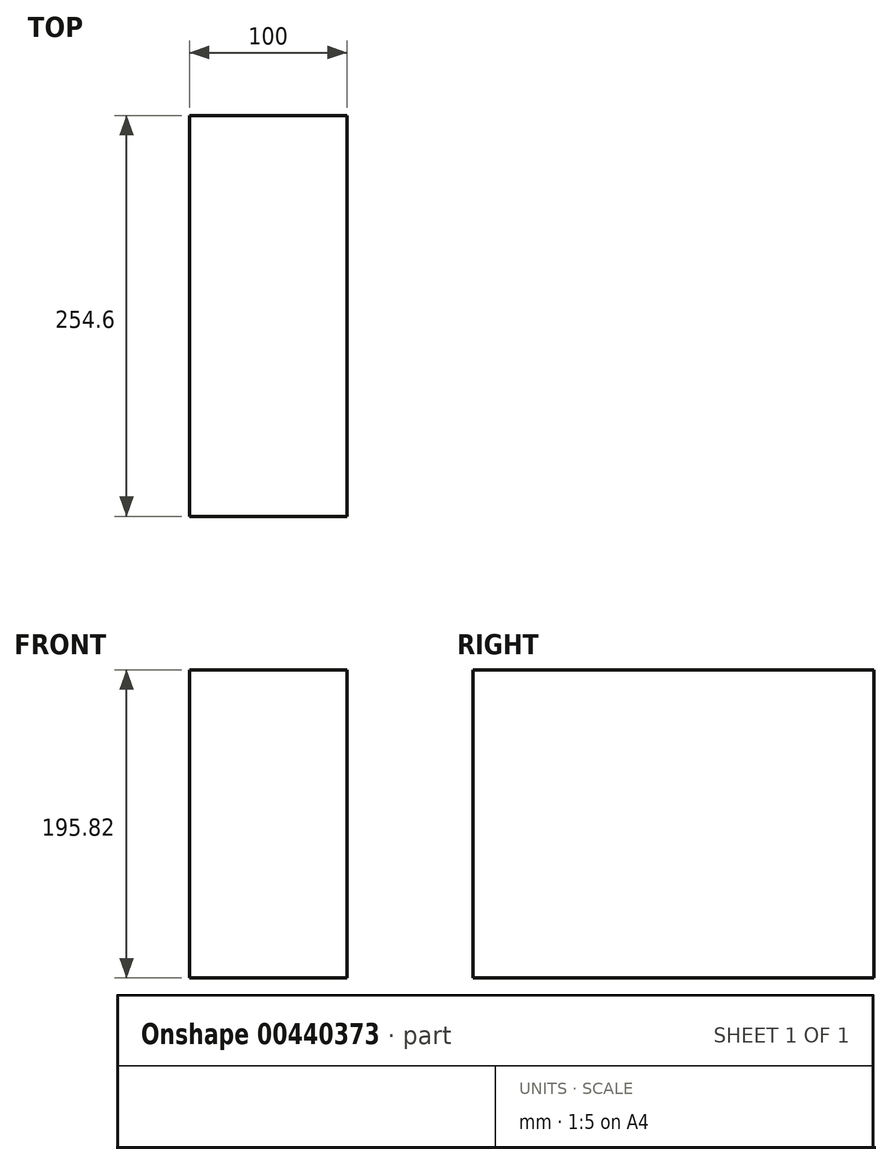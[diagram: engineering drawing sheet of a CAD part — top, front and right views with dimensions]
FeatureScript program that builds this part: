
annotation { "Feature Type Name" : "Feature", "Feature Type Description" : "" }
export const myFeature = defineFeature(function(context is Context, id is Id, definition is map)
    precondition{}
    {
        {
            var Q0;
            Q0=qCreatedBy(makeId("Right.planeOp"),FACE);
            var sketch = newSketch(context, id + "F0", { "sketchPlane" : qUnion([Q0])});
            skLineSegment(sketch, "E0.bottom", {"start": v(-86.9, 59.1) * mm, "end": v(107.7, 59.1) * mm});
            skLineSegment(sketch, "E0.top", {"start": v(-86.9, -56.73) * mm, "end": v(107.7, -56.73) * mm});
            skLineSegment(sketch, "E0.left", {"start": v(-86.9, 59.1) * mm, "end": v(-86.9, -56.73) * mm});
            skLineSegment(sketch, "E0.right", {"start": v(107.7, 59.1) * mm, "end": v(107.7, -56.73) * mm});
            skSolve(sketch);
        }
        {
            var Q0;
            Q0=makeQuery(id+"F0.imprint","IMPRINT",FACE,{"disambiguationData":[TD([[makeQuery(id+"F0.imprint","IMPRINT",EDGE,{"derivedFrom":sQuery(id+"F0.wireOp",EDGE,"E0.bottom")}),-1.0]])]});
            extrude(context, id + "F1", {"entities" : qUnion([Q0]), "depth" : 100 * mm});
        }
        {
            var Q0;
            Q0=makeQuery(id+"F1.opExtrude","SWEPT_FACE",FACE,{"disambiguationData":[OSD([sQuery(id+"F0.wireOp",EDGE,"E0.right")])]});
            extrude(context, id + "F2", {"entities" : qUnion([Q0]), "operationType" : NewBodyOperationType.ADD, "depth" : 60 * mm});
        }
        {
            var Q0;
            {var subQ0=sQuery(id+"F0.wireOp",EDGE,"E0.bottom");Q0=makeQuery(id+"F2.boolean.opBoolean","MERGE",FACE,{"derivedFrom":[makeQuery(id+"F1.opExtrude","SWEPT_FACE",FACE,{"disambiguationData":[OSD([subQ0])]}),makeQuery(id+"F2.opExtrude","SWEPT_FACE",FACE,{"disambiguationData":[OSD([subQ0,sQuery(id+"F0.wireOp",EDGE,"E0.right")])]})]});}
            extrude(context, id + "F3", {"entities" : qUnion([Q0]), "operationType" : NewBodyOperationType.ADD, "depth" : 80 * mm});
        }
    });
